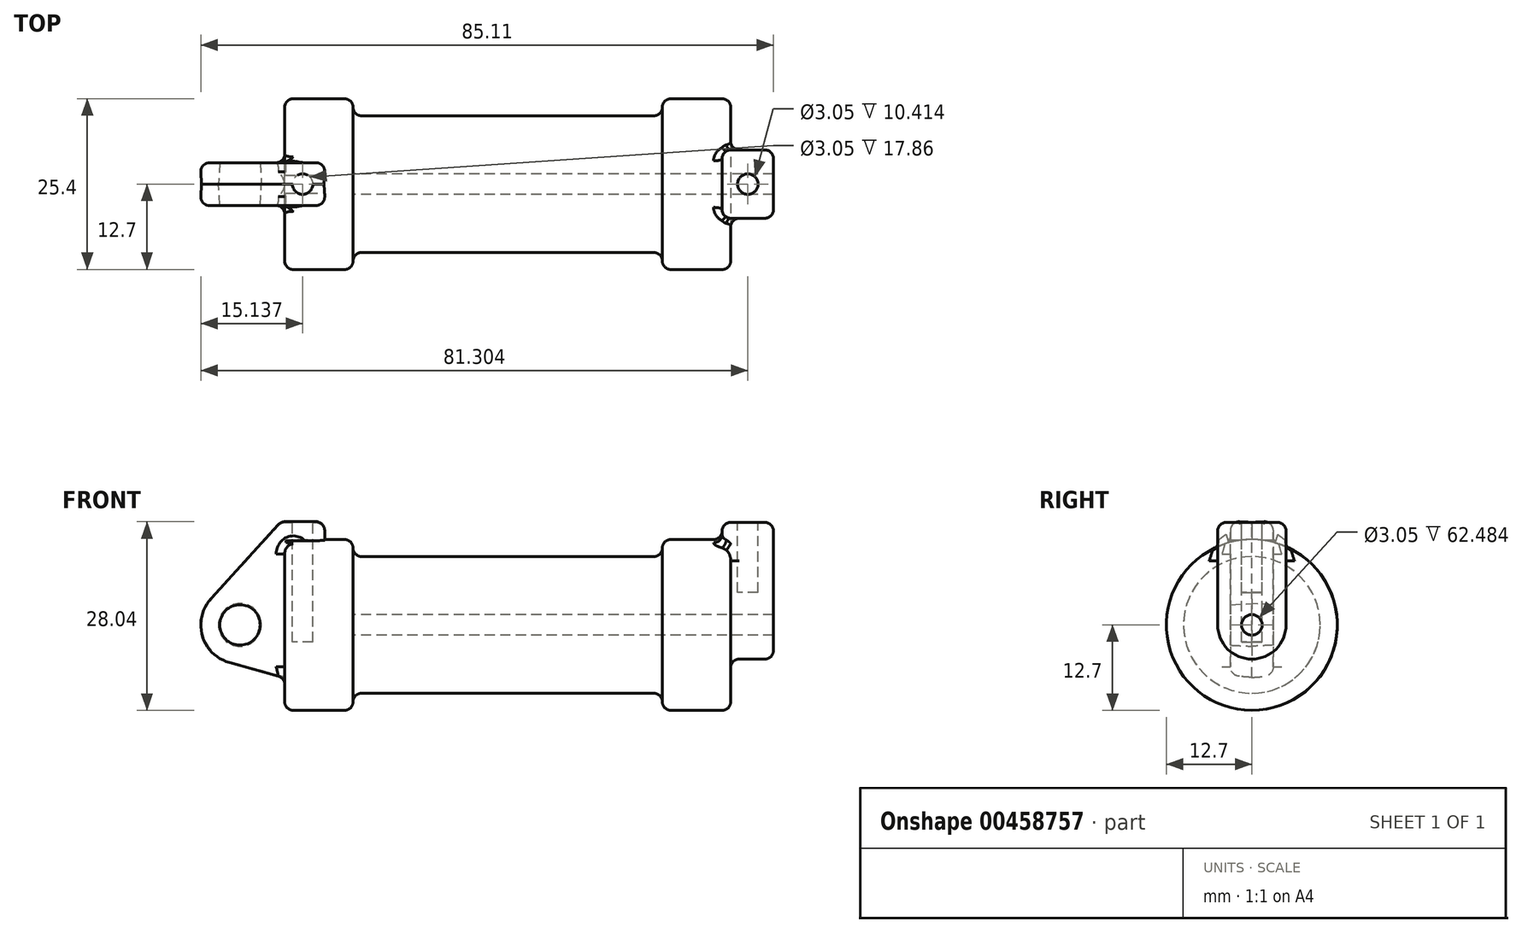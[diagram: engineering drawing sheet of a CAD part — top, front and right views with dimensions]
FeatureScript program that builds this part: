
annotation { "Feature Type Name" : "Feature", "Feature Type Description" : "" }
export const myFeature = defineFeature(function(context is Context, id is Id, definition is map)
    precondition{}
    {
        {
            var Q0;
            Q0=qCreatedBy(makeId("Front.planeOp"),FACE);
            var sketch = newSketch(context, id + "F0", { "sketchPlane" : qUnion([Q0])});
            skLineSegment(sketch, "E0", {"start": v(0, 0) * mm, "end": v(0, 12.7) * mm});
            skLineSegment(sketch, "E1", {"start": v(0, 12.7) * mm, "end": v(10.16, 12.7) * mm});
            skLineSegment(sketch, "E2", {"start": v(10.16, 12.7) * mm, "end": v(10.16, 10.16) * mm});
            skLineSegment(sketch, "E3", {"start": v(10.16, 10.16) * mm, "end": v(56.13, 10.16) * mm});
            skLineSegment(sketch, "E4", {"start": v(56.13, 10.16) * mm, "end": v(56.13, 12.7) * mm});
            skLineSegment(sketch, "E5", {"start": v(56.13, 12.7) * mm, "end": v(66.3, 12.7) * mm});
            skLineSegment(sketch, "E6", {"start": v(66.3, 12.7) * mm, "end": v(66.3, 0) * mm});
            skLineSegment(sketch, "E7", {"start": v(66.3, 0) * mm, "end": v(0, 0) * mm});
            skLineSegment(sketch, "E8", {"start": v(5.84, 15.24) * mm, "end": v(-0.5, 15.24) * mm});
            skLineSegment(sketch, "E9", {"start": v(-0.5, 15.24) * mm, "end": v(-10.88, 3.85) * mm});
            skLineSegment(sketch, "E10", {"start": v(0, 0) * mm, "end": v(-6.65, 0) * mm});
            skCircle(sketch, "E11", {"center": v(-6.65, 0) * mm, "radius": 5.72 * mm});
            skCircle(sketch, "E12", {"center": v(-6.65, 0) * mm, "radius": 3.18 * mm});
            skLineSegment(sketch, "E13", {"start": v(5.84, 15.24) * mm, "end": v(5.84, -9.4) * mm});
            skLineSegment(sketch, "E14", {"start": v(5.84, -9.4) * mm, "end": v(-8.18, -5.5) * mm});
            skLineSegment(sketch, "E15", {"start": v(0, 0) * mm, "end": v(0, -7.78) * mm});
            skSolve(sketch);
        }
        {
            var Q0;
            {var subQ0=sQuery(id+"F0.wireOp",EDGE,"E2");Q0=makeQuery(id+"F0.imprint","IMPRINT",FACE,{"disambiguationData":[TD([[makeQuery(id+"F0.imprint","IMPRINT",EDGE,{"derivedFrom":subQ0}),-1.0]])]});}
            var Q1;
            {var subQ0=sQuery(id+"F0.wireOp",EDGE,"E0");Q1=makeQuery(id+"F0.imprint","IMPRINT",FACE,{"disambiguationData":[TD([[makeQuery(id+"F0.imprint","IMPRINT",EDGE,{"derivedFrom":subQ0}),-1.0]])]});}
            var Q2;
            Q2=sQuery(id+"F0.wireOp",EDGE,"E7");
            revolve(context, id + "F1", {"entities" : qUnion([Q0, Q1]), "axis" : qUnion([Q2]), "revolveType" : RevolveType.FULL});
        }
        {
            var Q0;
            {var subQ1=sQuery(id+"F0.wireOp",EDGE,"E0");Q0=makeQuery(id+"F0.imprint","IMPRINT",FACE,{"disambiguationData":[TD([[makeQuery(id+"F0.imprint","IMPRINT",EDGE,{"derivedFrom":subQ1}),1.0]])]});}
            var Q1;
            {var subQ5=sQuery(id+"F0.wireOp",EDGE,"E12");Q1=makeQuery(id+"F0.imprint","IMPRINT",FACE,{"disambiguationData":[TD([[makeQuery(id+"F0.imprint","IMPRINT",EDGE,{"derivedFrom":subQ5}),-1.0]])]});}
            var Q2;
            {var subQ0=sQuery(id+"F0.wireOp",EDGE,"E15");Q2=makeQuery(id+"F0.imprint","IMPRINT",FACE,{"disambiguationData":[TD([[makeQuery(id+"F0.imprint","IMPRINT",EDGE,{"derivedFrom":subQ0}),-1.0]])]});}
            extrude(context, id + "F2", {"entities" : qUnion([Q0, Q1, Q2]), "operationType" : NewBodyOperationType.ADD, "depth" : 6.35 * mm, "hasDraft" : true, "draftAngle" : 3 * degree, "symmetric" : true});
        }
        {
            var Q0;
            Q0=makeQuery(id+"F1.opRevolve","SWEPT_FACE",FACE,{"disambiguationData":[OSD([sQuery(id+"F0.wireOp",EDGE,"E6")])]});
            var sketch = newSketch(context, id + "F3", { "sketchPlane" : qUnion([Q0])});
            skCircle(sketch, "E16", {"center": v(0, 0) * mm, "radius": 1.52 * mm});
            skCircle(sketch, "E17", {"center": v(0, 0) * mm, "radius": 5.08 * mm});
            skLineSegment(sketch, "E18", {"start": v(-5.08, 0) * mm, "end": v(-5.08, 15.24) * mm});
            skLineSegment(sketch, "E19", {"start": v(-5.08, 15.24) * mm, "end": v(5.08, 15.24) * mm});
            skLineSegment(sketch, "E20", {"start": v(5.08, 15.24) * mm, "end": v(5.08, 0) * mm});
            skSolve(sketch);
        }
        {
            var Q0;
            Q0=qSketchRegion(id+"F3",true);
            extrude(context, id + "F4", {"entities" : qUnion([Q0]), "operationType" : NewBodyOperationType.ADD, "depth" : 6.35 * mm});
        }
        {
            var Q0;
            Q0=qSketchRegion(id+"F3",true);
            extrude(context, id + "F5", {"entities" : qUnion([Q0]), "operationType" : NewBodyOperationType.ADD, "oppositeDirection" : true, "depth" : 1.27 * mm});
        }
        {
            var Q0;
            Q0=makeQuery(id+"F4.boolean.opBoolean","SPLIT",FACE,{"disambiguationData":[TD([makeQuery(id+"F4.opExtrude","SWEPT_FACE",FACE,{"disambiguationData":[OSD([sQuery(id+"F3.wireOp",EDGE,"E16")])]})])],"derivedFrom":makeQuery(id+"F1.opRevolve","SWEPT_FACE",FACE,{"disambiguationData":[OSD([sQuery(id+"F0.wireOp",EDGE,"E6")])]})});
            var Q1;
            Q1=makeQuery(id+"F1.opRevolve","SWEPT_FACE",FACE,{"disambiguationData":[OSD([sQuery(id+"F0.wireOp",EDGE,"E2")])]});
            extrude(context, id + "F6", {"entities" : qUnion([Q0]), "operationType" : NewBodyOperationType.REMOVE, "endBound" : BoundingType.UP_TO_SURFACE, "oppositeDirection" : true, "endBoundEntityFace" : qUnion([Q1]), "depth" : 25.4 * mm});
        }
        {
            var Q0;
            {var subQ0=sQuery(id+"F3.wireOp",EDGE,"E19");Q0=makeQuery(id+"F5.boolean.opBoolean","MERGE",FACE,{"derivedFrom":[makeQuery(id+"F4.opExtrude","SWEPT_FACE",FACE,{"disambiguationData":[OSD([subQ0])]}),makeQuery(id+"F5.opExtrude","SWEPT_FACE",FACE,{"disambiguationData":[OSD([subQ0])]})]});}
            var sketch = newSketch(context, id + "F7", { "sketchPlane" : qUnion([Q0])});
            skCircle(sketch, "E21", {"center": v(68.83, 0) * mm, "radius": 1.52 * mm});
            skPoint(sketch, "E22.endSnap0", {"position": v(65.02, 0) * mm});
            skSolve(sketch);
        }
        {
            var Q0;
            Q0=qSketchRegion(id+"F7",true);
            extrude(context, id + "F8", {"entities" : qUnion([Q0]), "operationType" : NewBodyOperationType.REMOVE, "oppositeDirection" : true, "depth" : 10.4 * mm});
        }
        {
            var Q0;
            {var subQ0=sQuery(id+"F3.wireOp",EDGE,"E19");Q0=makeQuery(id+"F5.boolean.opBoolean","MERGE",FACE,{"derivedFrom":[makeQuery(id+"F4.opExtrude","SWEPT_FACE",FACE,{"disambiguationData":[OSD([subQ0])]}),makeQuery(id+"F5.opExtrude","SWEPT_FACE",FACE,{"disambiguationData":[OSD([subQ0])]})]});}
            var sketch = newSketch(context, id + "F9", { "sketchPlane" : qUnion([Q0])});
            skLineSegment(sketch, "E23.0", {"start": v(5.84, 0) * mm, "end": v(-0.5, 0) * mm});
            skCircle(sketch, "E24", {"center": v(2.67, 0) * mm, "radius": 1.52 * mm});
            skSolve(sketch);
        }
        {
            var Q0;
            Q0=qSketchRegion(id+"F9",true);
            extrude(context, id + "F10", {"entities" : qUnion([Q0]), "operationType" : NewBodyOperationType.REMOVE, "oppositeDirection" : true, "depth" : 17.78 * mm, "hasSecondDirection" : true, "secondDirectionOppositeDirection" : false, "secondDirectionDepth" : 25.4 * mm});
        }
        {
            var Q0;
            Q0=makeQuery(id+"F1.opRevolve","SWEPT_EDGE",EDGE,{"disambiguationData":[OSD([sQuery(id+"F0.wireOp",EDGE,"E0"),sQuery(id+"F0.wireOp",EDGE,"E1")])]});
            var Q1;
            Q1=makeQuery(id+"F1.opRevolve","SWEPT_EDGE",EDGE,{"disambiguationData":[OSD([sQuery(id+"F0.wireOp",EDGE,"E1"),sQuery(id+"F0.wireOp",EDGE,"E2")])]});
            var Q2;
            Q2=makeQuery(id+"F1.opRevolve","SWEPT_EDGE",EDGE,{"disambiguationData":[OSD([sQuery(id+"F0.wireOp",EDGE,"E2"),sQuery(id+"F0.wireOp",EDGE,"E3")])]});
            var Q3;
            Q3=makeQuery(id+"F1.opRevolve","SWEPT_EDGE",EDGE,{"disambiguationData":[OSD([sQuery(id+"F0.wireOp",EDGE,"E4"),sQuery(id+"F0.wireOp",EDGE,"E5")])]});
            var Q4;
            Q4=makeQuery(id+"F1.opRevolve","SWEPT_EDGE",EDGE,{"disambiguationData":[OSD([sQuery(id+"F0.wireOp",EDGE,"E3"),sQuery(id+"F0.wireOp",EDGE,"E4")])]});
            var Q5;
            {var subQ0=sQuery(id+"F0.wireOp",EDGE,"E5");var subQ1=sQuery(id+"F0.wireOp",EDGE,"E6");Q5=makeQuery(id+"F4.boolean.opBoolean","SPLIT",EDGE,{"disambiguationData":[topologyDisambiguationEdgeConnected([makeQuery(id+"F1.opRevolve","SWEPT_FACE",FACE,{"disambiguationData":[OSD([subQ1])]})])],"derivedFrom":makeQuery(id+"F1.opRevolve","SWEPT_EDGE",EDGE,{"disambiguationData":[OSD([subQ0,subQ1])]})});}
            fillet(context, id + "F11", {"entities" : qUnion([Q0, Q1, Q2, Q3, Q4, Q5]), "radius" : 1.27 * mm, "tangentPropagation" : true, "allowEdgeOverflow" : false});
        }
        {
            var Q0;
            Q0=makeQuery(id+"F4.opExtrude","CAP_EDGE",EDGE,{"disambiguationData":[OSD([sQuery(id+"F3.wireOp",EDGE,"E19")])],"isStart":false});
            var Q1;
            Q1=makeQuery(id+"F4.opExtrude","CAP_EDGE",EDGE,{"disambiguationData":[OSD([sQuery(id+"F3.wireOp",EDGE,"E18")])],"isStart":false});
            var Q2;
            Q2=makeQuery(id+"F4.opExtrude","CAP_EDGE",EDGE,{"disambiguationData":[OSD([sQuery(id+"F3.wireOp",EDGE,"E17")])],"isStart":false});
            var Q3;
            Q3=makeQuery(id+"F4.opExtrude","CAP_EDGE",EDGE,{"disambiguationData":[OSD([sQuery(id+"F3.wireOp",EDGE,"E20")])],"isStart":false});
            var Q4;
            {var subQ0=sQuery(id+"F3.wireOp",EDGE,"E20");var subQ1=sQuery(id+"F3.wireOp",EDGE,"E19");Q4=makeQuery(id+"F5.boolean.opBoolean","MERGE",EDGE,{"derivedFrom":[makeQuery(id+"F4.opExtrude","SWEPT_EDGE",EDGE,{"disambiguationData":[OSD([subQ1,subQ0])]}),makeQuery(id+"F5.opExtrude","SWEPT_EDGE",EDGE,{"disambiguationData":[OSD([subQ1,subQ0])]})]});}
            var Q5;
            {var subQ0=sQuery(id+"F3.wireOp",EDGE,"E19");var subQ1=sQuery(id+"F3.wireOp",EDGE,"E18");Q5=makeQuery(id+"F5.boolean.opBoolean","MERGE",EDGE,{"derivedFrom":[makeQuery(id+"F4.opExtrude","SWEPT_EDGE",EDGE,{"disambiguationData":[OSD([subQ1,subQ0])]}),makeQuery(id+"F5.opExtrude","SWEPT_EDGE",EDGE,{"disambiguationData":[OSD([subQ1,subQ0])]})]});}
            var Q6;
            Q6=makeQuery(id+"F5.opExtrude","CAP_EDGE",EDGE,{"disambiguationData":[OSD([sQuery(id+"F3.wireOp",EDGE,"E19")])],"isStart":false});
            var Q7;
            Q7=makeQuery(id+"F5.boolean.opBoolean","INTERSECT",EDGE,{"derivedFrom":[makeQuery(id+"F1.opRevolve","SWEPT_FACE",FACE,{"disambiguationData":[OSD([sQuery(id+"F0.wireOp",EDGE,"E5")])]}),makeQuery(id+"F5.opExtrude","CAP_FACE",FACE,{"disambiguationData":[OSD([sQuery(id+"F3.wireOp",EDGE,"E16"),sQuery(id+"F3.wireOp",EDGE,"E17"),sQuery(id+"F3.wireOp",EDGE,"E18"),sQuery(id+"F3.wireOp",EDGE,"E19"),sQuery(id+"F3.wireOp",EDGE,"E20")])],"isStart":false})]});
            var Q8;
            Q8=makeQuery(id+"F5.opExtrude","CAP_EDGE",EDGE,{"disambiguationData":[OSD([sQuery(id+"F3.wireOp",EDGE,"E20")])],"isStart":false});
            var Q9;
            {var subQ0=sQuery(id+"F3.wireOp",EDGE,"E20");var subQ1=sQuery(id+"F0.wireOp",EDGE,"E5");var subQ2=sQuery(id+"F0.wireOp",EDGE,"E6");Q9=makeQuery(id+"F11.opFillet","BLEND_EDGE",EDGE,{"blendedFrom":[makeQuery(id+"F4.boolean.opBoolean","SPLIT",EDGE,{"disambiguationData":[topologyDisambiguationEdgeConnected([makeQuery(id+"F1.opRevolve","SWEPT_FACE",FACE,{"disambiguationData":[OSD([subQ2])]})])],"derivedFrom":makeQuery(id+"F1.opRevolve","SWEPT_EDGE",EDGE,{"disambiguationData":[OSD([subQ1,subQ2])]})}),makeQuery(id+"F5.boolean.opBoolean","MERGE",FACE,{"derivedFrom":[makeQuery(id+"F4.opExtrude","SWEPT_FACE",FACE,{"disambiguationData":[OSD([subQ0])]}),makeQuery(id+"F5.opExtrude","SWEPT_FACE",FACE,{"disambiguationData":[OSD([subQ0])]})]})],"blendedInto":[makeQuery(id+"F5.boolean.opBoolean","MERGE",FACE,{"derivedFrom":[makeQuery(id+"F4.opExtrude","SWEPT_FACE",FACE,{"disambiguationData":[OSD([subQ0])]}),makeQuery(id+"F5.opExtrude","SWEPT_FACE",FACE,{"disambiguationData":[OSD([subQ0])]})]})]});}
            var Q10;
            Q10=makeQuery(id+"F5.opExtrude","CAP_EDGE",EDGE,{"disambiguationData":[OSD([sQuery(id+"F3.wireOp",EDGE,"E18")])],"isStart":false});
            fillet(context, id + "F12", {"entities" : qUnion([Q0, Q1, Q2, Q3, Q4, Q5, Q6, Q7, Q8, Q9, Q10]), "radius" : 1.27 * mm, "tangentPropagation" : true, "allowEdgeOverflow" : false});
        }
        {
            var Q0;
            {var subQ0=sQuery(id+"F0.wireOp",EDGE,"E0");Q0=makeQuery(id+"F2.boolean.opBoolean","INTERSECT",EDGE,{"derivedFrom":[makeQuery(id+"F1.opRevolve","SWEPT_FACE",FACE,{"disambiguationData":[OSD([subQ0])]}),makeQuery(id+"F2.opExtrude","CAP_FACE",FACE,{"disambiguationData":[OSD([subQ0,sQuery(id+"F0.wireOp",EDGE,"E1"),sQuery(id+"F0.wireOp",EDGE,"E8"),sQuery(id+"F0.wireOp",EDGE,"E9"),sQuery(id+"F0.wireOp",EDGE,"E11"),sQuery(id+"F0.wireOp",EDGE,"E12"),sQuery(id+"F0.wireOp",EDGE,"E13"),sQuery(id+"F0.wireOp",EDGE,"E14"),sQuery(id+"F0.wireOp",EDGE,"E15")])],"isStart":false})]});}
            var Q1;
            Q1=makeQuery(id+"F2.opExtrude","CAP_EDGE",EDGE,{"disambiguationData":[OSD([sQuery(id+"F0.wireOp",EDGE,"E14")])],"isStart":false});
            var Q2;
            Q2=makeQuery(id+"F2.opExtrude","CAP_EDGE",EDGE,{"disambiguationData":[OSD([sQuery(id+"F0.wireOp",EDGE,"E14")])],"isStart":true});
            var Q3;
            {var subQ0=sQuery(id+"F0.wireOp",EDGE,"E0");Q3=makeQuery(id+"F2.boolean.opBoolean","INTERSECT",EDGE,{"derivedFrom":[makeQuery(id+"F1.opRevolve","SWEPT_FACE",FACE,{"disambiguationData":[OSD([subQ0])]}),makeQuery(id+"F2.opExtrude","CAP_FACE",FACE,{"disambiguationData":[OSD([subQ0,sQuery(id+"F0.wireOp",EDGE,"E1"),sQuery(id+"F0.wireOp",EDGE,"E8"),sQuery(id+"F0.wireOp",EDGE,"E9"),sQuery(id+"F0.wireOp",EDGE,"E11"),sQuery(id+"F0.wireOp",EDGE,"E12"),sQuery(id+"F0.wireOp",EDGE,"E13"),sQuery(id+"F0.wireOp",EDGE,"E14"),sQuery(id+"F0.wireOp",EDGE,"E15")])],"isStart":true})]});}
            var Q4;
            Q4=makeQuery(id+"F2.*.split.splitOp","SPLIT",EDGE,{"derivedFrom":makeQuery(id+"F2.opExtrude","SWEPT_EDGE",EDGE,{"disambiguationData":[OSD([sQuery(id+"F0.wireOp",EDGE,"E8"),sQuery(id+"F0.wireOp",EDGE,"E9")])]})});
            var Q5;
            Q5=makeQuery(id+"F2.*.split.splitOp","SPLIT",EDGE,{"derivedFrom":makeQuery(id+"F2.opExtrude","SWEPT_EDGE",EDGE,{"disambiguationData":[OSD([sQuery(id+"F0.wireOp",EDGE,"E8"),sQuery(id+"F0.wireOp",EDGE,"E9")])]}),"isFromBackBody":true});
            var Q6;
            Q6=makeQuery(id+"F2.opExtrude","CAP_EDGE",EDGE,{"disambiguationData":[OSD([sQuery(id+"F0.wireOp",EDGE,"E8")])],"isStart":true});
            var Q7;
            Q7=makeQuery(id+"F2.opExtrude","CAP_EDGE",EDGE,{"disambiguationData":[OSD([sQuery(id+"F0.wireOp",EDGE,"E8")])],"isStart":false});
            var Q8;
            Q8=makeQuery(id+"F2.opExtrude","CAP_EDGE",EDGE,{"disambiguationData":[OSD([sQuery(id+"F0.wireOp",EDGE,"E13")])],"isStart":false});
            var Q9;
            Q9=makeQuery(id+"F2.opExtrude","CAP_EDGE",EDGE,{"disambiguationData":[OSD([sQuery(id+"F0.wireOp",EDGE,"E13")])],"isStart":true});
            var Q10;
            Q10=makeQuery(id+"F2.*.split.splitOp","SPLIT",EDGE,{"derivedFrom":makeQuery(id+"F2.opExtrude","SWEPT_EDGE",EDGE,{"disambiguationData":[OSD([sQuery(id+"F0.wireOp",EDGE,"E8"),sQuery(id+"F0.wireOp",EDGE,"E13")])]}),"isFromBackBody":true});
            var Q11;
            Q11=makeQuery(id+"F2.*.split.splitOp","SPLIT",EDGE,{"derivedFrom":makeQuery(id+"F2.opExtrude","SWEPT_EDGE",EDGE,{"disambiguationData":[OSD([sQuery(id+"F0.wireOp",EDGE,"E8"),sQuery(id+"F0.wireOp",EDGE,"E13")])]})});
            fillet(context, id + "F13", {"entities" : qUnion([Q0, Q1, Q2, Q3, Q4, Q5, Q6, Q7, Q8, Q9, Q10, Q11]), "radius" : 1.27 * mm, "tangentPropagation" : true, "allowEdgeOverflow" : false});
        }
    });
